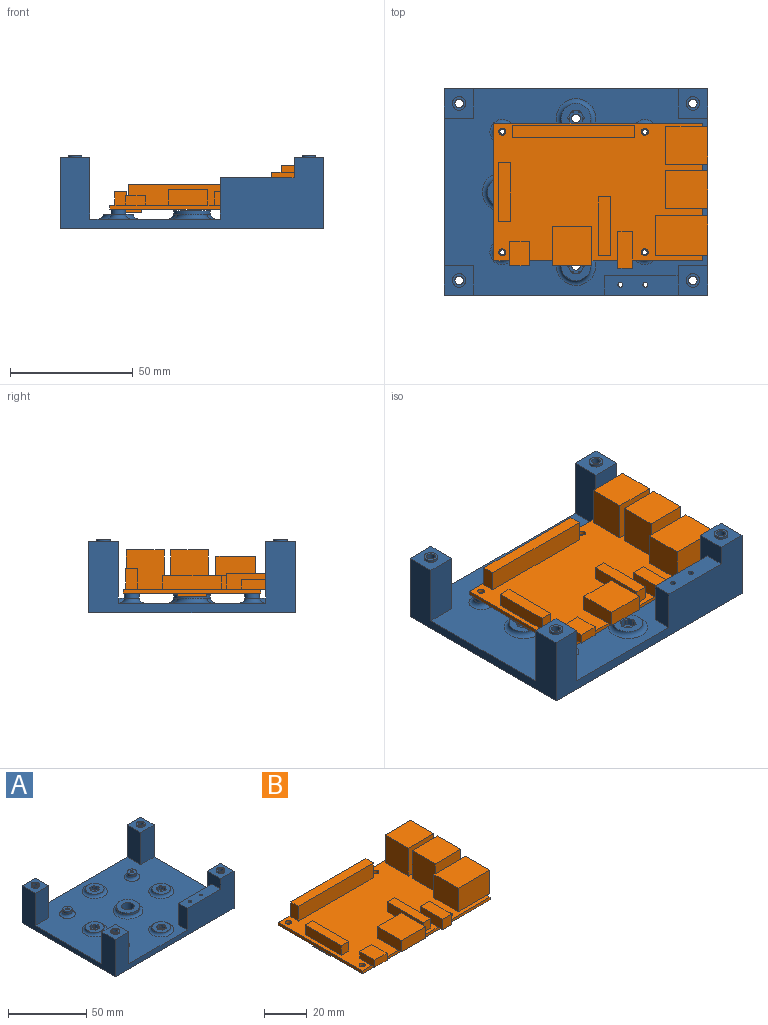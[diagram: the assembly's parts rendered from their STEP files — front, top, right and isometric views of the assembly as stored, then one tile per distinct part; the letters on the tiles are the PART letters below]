
ASSEMBLY  parts=2 mates=1
PART A: 277 faces, bbox 107x84x30 mm
  f0: plane 107x84mm, normal (0,0,1), area 6770.1mm2, adj f1,f2,f3,f4,f9,f24,f55,f56
  f1: plane 25x12mm, normal (-1,0,0), area 165.6mm2, adj f0,f4,f23,f24,f272,f274
  f2: plane 107x29mm, normal (0,1,0), area 1028mm2, adj f0,f3,f9,f10,f54,f55,f118,f119
  f3: plane 84x29mm, normal (-1,0,0), area 936mm2, adj f0,f2,f4,f10,f86,f88,f118,f120
  f4: plane 107x29mm, normal (0,-1,0), area 1532mm2, adj f0,f1,f3,f9,f10,f23,f86,f87
  f5: cylinder r=1mm len=8mm, axis (0,0,1), area 50.3mm2, adj f10,f11
  f6: cylinder r=1mm len=8mm, axis (0,0,1), area 50.3mm2, adj f10,f17
  f7: cylinder r=1mm len=8mm, axis (0,0,1), area 50.3mm2, adj f10,f13
  f8: cylinder r=1mm len=8mm, axis (0,0,1), area 50.3mm2, adj f10,f15
  f9: plane 84x29mm, normal (1,0,0), area 936mm2, adj f0,f2,f4,f10,f23,f24,f54,f56
  f10: plane 107x84mm, normal (0,0,-1), area 8651.1mm2, adj f2,f3,f4,f5,f6,f7,f8,f9
  f11: plane 6x6mm, normal (0,0,1), area 25.1mm2, adj f5,f12
  f12: cylinder r=3mm len=6mm, axis (0,0,-1), area 37.7mm2, adj f11,f263
  f13: plane 6x6mm, normal (0,0,1), area 25.1mm2, adj f7,f14
  f14: cylinder r=3mm len=6mm, axis (0,0,-1), area 37.7mm2, adj f13,f266
  f15: plane 6x6mm, normal (0,0,1), area 25.1mm2, adj f8,f16
  f16: cylinder r=3mm len=6mm, axis (0,0,-1), area 37.7mm2, adj f15,f265
  f17: plane 6x6mm, normal (0,0,1), area 25.1mm2, adj f6,f18
  f18: cylinder r=3mm len=6mm, axis (0,0,-1), area 37.7mm2, adj f17,f264
  f19: cylinder r=4mm len=22mm, axis (0,0,-1), area 552.9mm2, adj f10,f83
  f20: cylinder r=4mm len=22mm, axis (0,0,-1), area 552.9mm2, adj f10,f115
  f21: cylinder r=4mm len=22mm, axis (0,0,-1), area 552.9mm2, adj f10,f147
  f22: cylinder r=4mm len=22mm, axis (0,0,-1), area 552.9mm2, adj f10,f51
  f23: plane 12x12mm, normal (0,0,1), area 120.2mm2, adj f1,f4,f9,f24,f52
  f24: plane 25x12mm, normal (0,1,0), area 300mm2, adj f0,f1,f9,f23
  f25: plane 3x2.96mm, normal (0,1,0), area 6.4mm2, adj f31,f32,f33,f40,f41,f42,f49,f51
  f26: plane 3x2.57mm, normal (-0.87,0.5,0), area 6.4mm2, adj f31,f32,f33,f37,f38,f39,f49,f51
  f27: plane 3x2.57mm, normal (-0.87,-0.5,0), area 6.4mm2, adj f34,f35,f36,f37,f38,f39,f49,f51
  f28: plane 3x2.96mm, normal (0,-1,0), area 6.4mm2, adj f34,f35,f36,f46,f47,f48,f49,f51
  f29: plane 3x2.57mm, normal (0.87,-0.5,0), area 6.4mm2, adj f43,f44,f45,f46,f47,f48,f49,f51
  f30: plane 3x2.57mm, normal (0.87,0.5,0), area 6.4mm2, adj f40,f41,f42,f43,f44,f45,f49,f51
  f31: cylinder r=0.75mm len=2mm, axis (0,0,-1), area 3.1mm2, adj f25,f26,f32,f33
  f32: cone r=0.25mm half-angle=45deg, axis (0,0,-1), area 0.7mm2, adj f25,f26,f31,f49
  f33: cone r=0.75mm half-angle=45deg, axis (0,0,1), area 0.7mm2, adj f25,f26,f31,f51
  f34: cylinder r=0.75mm len=2mm, axis (0,0,-1), area 3.1mm2, adj f27,f28,f35,f36
  f35: cone r=0.25mm half-angle=45deg, axis (0,0,-1), area 0.7mm2, adj f27,f28,f34,f49
  f36: cone r=0.75mm half-angle=45deg, axis (0,0,1), area 0.7mm2, adj f27,f28,f34,f51
  f37: cone r=0.75mm half-angle=45deg, axis (0,0,1), area 0.7mm2, adj f26,f27,f39,f51
  f38: cone r=0.25mm half-angle=45deg, axis (0,0,-1), area 0.7mm2, adj f26,f27,f39,f49
  f39: cylinder r=0.75mm len=2mm, axis (0,0,-1), area 3.1mm2, adj f26,f27,f37,f38
  f40: cone r=0.75mm half-angle=45deg, axis (0,0,1), area 0.7mm2, adj f25,f30,f42,f51
  f41: cone r=0.25mm half-angle=45deg, axis (0,0,-1), area 0.7mm2, adj f25,f30,f42,f49
  f42: cylinder r=0.75mm len=2mm, axis (0,0,-1), area 3.1mm2, adj f25,f30,f40,f41
  f43: cone r=0.75mm half-angle=45deg, axis (0,0,1), area 0.7mm2, adj f29,f30,f45,f51
  f44: cone r=0.25mm half-angle=45deg, axis (0,0,-1), area 0.7mm2, adj f29,f30,f45,f49
  f45: cylinder r=0.75mm len=2mm, axis (0,0,-1), area 3.1mm2, adj f29,f30,f43,f44
  f46: cone r=0.75mm half-angle=45deg, axis (0,0,1), area 0.7mm2, adj f28,f29,f48,f51
  f47: cone r=0.25mm half-angle=45deg, axis (0,0,-1), area 0.7mm2, adj f28,f29,f48,f49
  f48: cylinder r=0.75mm len=2mm, axis (0,0,-1), area 3.1mm2, adj f28,f29,f46,f47
  f49: plane 6.68x6mm, normal (0,0,-1), area 21.2mm2, adj f25,f26,f27,f28,f29,f30,f32,f35
  f50: cylinder r=1.75mm len=5mm, axis (0,0,1), area 55mm2, adj f49,f53
  f51: plane 8x8mm, normal (0,0,-1), area 19.5mm2, adj f22,f25,f26,f27,f28,f29,f30,f33
  f52: cylinder r=2.75mm len=5.5mm, axis (0,0,-1), area 17.3mm2, adj f23,f53
  f53: plane 5.5x5.5mm, normal (0,0,1), area 14.1mm2, adj f50,f52
  f54: plane 12x12mm, normal (0,0,1), area 120.2mm2, adj f2,f9,f55,f56,f84
  f55: plane 25x12mm, normal (-1,0,0), area 300mm2, adj f0,f2,f54,f56
  f56: plane 25x12mm, normal (0,-1,0), area 300mm2, adj f0,f9,f54,f55
  f57: plane 3x2.96mm, normal (0,-1,0), area 6.4mm2, adj f63,f64,f65,f72,f73,f74,f81,f83
  f58: plane 3x2.57mm, normal (-0.87,-0.5,0), area 6.4mm2, adj f63,f64,f65,f69,f70,f71,f81,f83
  f59: plane 3x2.57mm, normal (-0.87,0.5,0), area 6.4mm2, adj f66,f67,f68,f69,f70,f71,f81,f83
  f60: plane 3x2.96mm, normal (0,1,0), area 6.4mm2, adj f66,f67,f68,f78,f79,f80,f81,f83
  f61: plane 3x2.57mm, normal (0.87,0.5,0), area 6.4mm2, adj f75,f76,f77,f78,f79,f80,f81,f83
  f62: plane 3x2.57mm, normal (0.87,-0.5,0), area 6.4mm2, adj f72,f73,f74,f75,f76,f77,f81,f83
  f63: cylinder r=0.75mm len=2mm, axis (0,0,-1), area 3.1mm2, adj f57,f58,f64,f65
  f64: cone r=0.25mm half-angle=45deg, axis (0,0,-1), area 0.7mm2, adj f57,f58,f63,f81
  f65: cone r=0.75mm half-angle=45deg, axis (0,0,1), area 0.7mm2, adj f57,f58,f63,f83
  f66: cylinder r=0.75mm len=2mm, axis (0,0,-1), area 3.1mm2, adj f59,f60,f67,f68
  f67: cone r=0.25mm half-angle=45deg, axis (0,0,-1), area 0.7mm2, adj f59,f60,f66,f81
  f68: cone r=0.75mm half-angle=45deg, axis (0,0,1), area 0.7mm2, adj f59,f60,f66,f83
  f69: cone r=0.75mm half-angle=45deg, axis (0,0,1), area 0.7mm2, adj f58,f59,f71,f83
  f70: cone r=0.25mm half-angle=45deg, axis (0,0,-1), area 0.7mm2, adj f58,f59,f71,f81
  f71: cylinder r=0.75mm len=2mm, axis (0,0,-1), area 3.1mm2, adj f58,f59,f69,f70
  f72: cone r=0.75mm half-angle=45deg, axis (0,0,1), area 0.7mm2, adj f57,f62,f74,f83
  f73: cone r=0.25mm half-angle=45deg, axis (0,0,-1), area 0.7mm2, adj f57,f62,f74,f81
  f74: cylinder r=0.75mm len=2mm, axis (0,0,-1), area 3.1mm2, adj f57,f62,f72,f73
  f75: cone r=0.75mm half-angle=45deg, axis (0,0,1), area 0.7mm2, adj f61,f62,f77,f83
  f76: cone r=0.25mm half-angle=45deg, axis (0,0,-1), area 0.7mm2, adj f61,f62,f77,f81
  f77: cylinder r=0.75mm len=2mm, axis (0,0,-1), area 3.1mm2, adj f61,f62,f75,f76
  f78: cone r=0.75mm half-angle=45deg, axis (0,0,1), area 0.7mm2, adj f60,f61,f80,f83
  f79: cone r=0.25mm half-angle=45deg, axis (0,0,-1), area 0.7mm2, adj f60,f61,f80,f81
  f80: cylinder r=0.75mm len=2mm, axis (0,0,-1), area 3.1mm2, adj f60,f61,f78,f79
  f81: plane 6.68x6mm, normal (0,0,-1), area 21.2mm2, adj f57,f58,f59,f60,f61,f62,f64,f67
  f82: cylinder r=1.75mm len=5mm, axis (0,0,1), area 55mm2, adj f81,f85
  f83: plane 8x8mm, normal (0,0,-1), area 19.5mm2, adj f19,f57,f58,f59,f60,f61,f62,f65
  f84: cylinder r=2.75mm len=5.5mm, axis (0,0,-1), area 17.3mm2, adj f54,f85
  f85: plane 5.5x5.5mm, normal (0,0,1), area 14.1mm2, adj f82,f84
  f86: plane 12x12mm, normal (0,0,1), area 120.2mm2, adj f3,f4,f87,f88,f116
  f87: plane 25x12mm, normal (1,0,0), area 300mm2, adj f0,f4,f86,f88
  f88: plane 25x12mm, normal (0,1,0), area 300mm2, adj f0,f3,f86,f87
  f89: plane 3x2.96mm, normal (0,1,0), area 6.4mm2, adj f95,f96,f97,f104,f105,f106,f113,f115
  f90: plane 3x2.57mm, normal (0.87,0.5,0), area 6.4mm2, adj f95,f96,f97,f101,f102,f103,f113,f115
  f91: plane 3x2.57mm, normal (0.87,-0.5,0), area 6.4mm2, adj f98,f99,f100,f101,f102,f103,f113,f115
  f92: plane 3x2.96mm, normal (0,-1,0), area 6.4mm2, adj f98,f99,f100,f110,f111,f112,f113,f115
  f93: plane 3x2.57mm, normal (-0.87,-0.5,0), area 6.4mm2, adj f107,f108,f109,f110,f111,f112,f113,f115
  f94: plane 3x2.57mm, normal (-0.87,0.5,0), area 6.4mm2, adj f104,f105,f106,f107,f108,f109,f113,f115
  f95: cylinder r=0.75mm len=2mm, axis (0,0,-1), area 3.1mm2, adj f89,f90,f96,f97
  f96: cone r=0.25mm half-angle=45deg, axis (0,0,-1), area 0.7mm2, adj f89,f90,f95,f113
  f97: cone r=0.75mm half-angle=45deg, axis (0,0,1), area 0.7mm2, adj f89,f90,f95,f115
  f98: cylinder r=0.75mm len=2mm, axis (0,0,-1), area 3.1mm2, adj f91,f92,f99,f100
  f99: cone r=0.25mm half-angle=45deg, axis (0,0,-1), area 0.7mm2, adj f91,f92,f98,f113
  f100: cone r=0.75mm half-angle=45deg, axis (0,0,1), area 0.7mm2, adj f91,f92,f98,f115
  f101: cone r=0.75mm half-angle=45deg, axis (0,0,1), area 0.7mm2, adj f90,f91,f103,f115
  f102: cone r=0.25mm half-angle=45deg, axis (0,0,-1), area 0.7mm2, adj f90,f91,f103,f113
  f103: cylinder r=0.75mm len=2mm, axis (0,0,-1), area 3.1mm2, adj f90,f91,f101,f102
  f104: cone r=0.75mm half-angle=45deg, axis (0,0,1), area 0.7mm2, adj f89,f94,f106,f115
  f105: cone r=0.25mm half-angle=45deg, axis (0,0,-1), area 0.7mm2, adj f89,f94,f106,f113
  f106: cylinder r=0.75mm len=2mm, axis (0,0,-1), area 3.1mm2, adj f89,f94,f104,f105
  f107: cone r=0.75mm half-angle=45deg, axis (0,0,1), area 0.7mm2, adj f93,f94,f109,f115
  f108: cone r=0.25mm half-angle=45deg, axis (0,0,-1), area 0.7mm2, adj f93,f94,f109,f113
  f109: cylinder r=0.75mm len=2mm, axis (0,0,-1), area 3.1mm2, adj f93,f94,f107,f108
  f110: cone r=0.75mm half-angle=45deg, axis (0,0,1), area 0.7mm2, adj f92,f93,f112,f115
  f111: cone r=0.25mm half-angle=45deg, axis (0,0,-1), area 0.7mm2, adj f92,f93,f112,f113
  f112: cylinder r=0.75mm len=2mm, axis (0,0,-1), area 3.1mm2, adj f92,f93,f110,f111
  f113: plane 6.68x6mm, normal (0,0,-1), area 21.2mm2, adj f89,f90,f91,f92,f93,f94,f96,f99
  f114: cylinder r=1.75mm len=5mm, axis (0,0,1), area 55mm2, adj f113,f117
  f115: plane 8x8mm, normal (0,0,-1), area 19.5mm2, adj f20,f89,f90,f91,f92,f93,f94,f97
  f116: cylinder r=2.75mm len=5.5mm, axis (0,0,-1), area 17.3mm2, adj f86,f117
  f117: plane 5.5x5.5mm, normal (0,0,1), area 14.1mm2, adj f114,f116
  f118: plane 12x12mm, normal (0,0,1), area 120.2mm2, adj f2,f3,f119,f120,f148
  f119: plane 25x12mm, normal (1,0,0), area 300mm2, adj f0,f2,f118,f120
  f120: plane 25x12mm, normal (0,-1,0), area 300mm2, adj f0,f3,f118,f119
  f121: plane 3x2.96mm, normal (0,-1,0), area 6.4mm2, adj f127,f128,f129,f136,f137,f138,f145,f147
  f122: plane 3x2.57mm, normal (0.87,-0.5,0), area 6.4mm2, adj f127,f128,f129,f133,f134,f135,f145,f147
  f123: plane 3x2.57mm, normal (0.87,0.5,0), area 6.4mm2, adj f130,f131,f132,f133,f134,f135,f145,f147
  f124: plane 3x2.96mm, normal (0,1,0), area 6.4mm2, adj f130,f131,f132,f142,f143,f144,f145,f147
  f125: plane 3x2.57mm, normal (-0.87,0.5,0), area 6.4mm2, adj f139,f140,f141,f142,f143,f144,f145,f147
  f126: plane 3x2.57mm, normal (-0.87,-0.5,0), area 6.4mm2, adj f136,f137,f138,f139,f140,f141,f145,f147
  f127: cylinder r=0.75mm len=2mm, axis (0,0,-1), area 3.1mm2, adj f121,f122,f128,f129
  f128: cone r=0.25mm half-angle=45deg, axis (0,0,-1), area 0.7mm2, adj f121,f122,f127,f145
  f129: cone r=0.75mm half-angle=45deg, axis (0,0,1), area 0.7mm2, adj f121,f122,f127,f147
  f130: cylinder r=0.75mm len=2mm, axis (0,0,-1), area 3.1mm2, adj f123,f124,f131,f132
  f131: cone r=0.25mm half-angle=45deg, axis (0,0,-1), area 0.7mm2, adj f123,f124,f130,f145
  f132: cone r=0.75mm half-angle=45deg, axis (0,0,1), area 0.7mm2, adj f123,f124,f130,f147
  f133: cone r=0.75mm half-angle=45deg, axis (0,0,1), area 0.7mm2, adj f122,f123,f135,f147
  f134: cone r=0.25mm half-angle=45deg, axis (0,0,-1), area 0.7mm2, adj f122,f123,f135,f145
  f135: cylinder r=0.75mm len=2mm, axis (0,0,-1), area 3.1mm2, adj f122,f123,f133,f134
  f136: cone r=0.75mm half-angle=45deg, axis (0,0,1), area 0.7mm2, adj f121,f126,f138,f147
  f137: cone r=0.25mm half-angle=45deg, axis (0,0,-1), area 0.7mm2, adj f121,f126,f138,f145
  f138: cylinder r=0.75mm len=2mm, axis (0,0,-1), area 3.1mm2, adj f121,f126,f136,f137
  f139: cone r=0.75mm half-angle=45deg, axis (0,0,1), area 0.7mm2, adj f125,f126,f141,f147
  f140: cone r=0.25mm half-angle=45deg, axis (0,0,-1), area 0.7mm2, adj f125,f126,f141,f145
  f141: cylinder r=0.75mm len=2mm, axis (0,0,-1), area 3.1mm2, adj f125,f126,f139,f140
  f142: cone r=0.75mm half-angle=45deg, axis (0,0,1), area 0.7mm2, adj f124,f125,f144,f147
  f143: cone r=0.25mm half-angle=45deg, axis (0,0,-1), area 0.7mm2, adj f124,f125,f144,f145
  f144: cylinder r=0.75mm len=2mm, axis (0,0,-1), area 3.1mm2, adj f124,f125,f142,f143
  f145: plane 6.68x6mm, normal (0,0,-1), area 21.2mm2, adj f121,f122,f123,f124,f125,f126,f128,f131
  f146: cylinder r=1.75mm len=5mm, axis (0,0,1), area 55mm2, adj f145,f149
  f147: plane 8x8mm, normal (0,0,-1), area 19.5mm2, adj f21,f121,f122,f123,f124,f125,f126,f129
  f148: cylinder r=2.75mm len=5.5mm, axis (0,0,-1), area 17.3mm2, adj f118,f149
  f149: plane 5.5x5.5mm, normal (0,0,1), area 14.1mm2, adj f146,f148
  f150: plane 15x15mm, normal (0,0,1), area 126.4mm2, adj f151,f152
  f151: cylinder r=7.5mm len=15mm, axis (0,0,1), area 61.3mm2, adj f150,f267
  f152: cylinder r=4mm len=8mm, axis (0,0,1), area 138.2mm2, adj f150,f153
  f153: plane 10x10mm, normal (0,0,-1), area 28.3mm2, adj f152,f154
  f154: cylinder r=5mm len=10mm, axis (0,0,1), area 56.5mm2, adj f10,f153
  f155: plane 12x12mm, normal (0,0,1), area 82.3mm2, adj f156,f157,f158,f159,f160,f161,f163,f166
  f156: plane 3x2.96mm, normal (0,-1,0), area 6.4mm2, adj f155,f162,f163,f164,f171,f172,f173,f180
  f157: plane 3x2.57mm, normal (-0.87,-0.5,0), area 6.4mm2, adj f155,f162,f163,f164,f168,f169,f170,f180
  f158: plane 3x2.57mm, normal (-0.87,0.5,0), area 6.4mm2, adj f155,f165,f166,f167,f168,f169,f170,f180
  f159: plane 3x2.96mm, normal (0,1,0), area 6.4mm2, adj f155,f165,f166,f167,f177,f178,f179,f180
  f160: plane 3x2.57mm, normal (0.87,0.5,0), area 6.4mm2, adj f155,f174,f175,f176,f177,f178,f179,f180
  f161: plane 3x2.57mm, normal (0.87,-0.5,0), area 6.4mm2, adj f155,f171,f172,f173,f174,f175,f176,f180
  f162: cylinder r=0.75mm len=2mm, axis (0,0,-1), area 3.1mm2, adj f156,f157,f163,f164
  f163: cone r=0.25mm half-angle=45deg, axis (0,0,-1), area 0.7mm2, adj f155,f156,f157,f162
  f164: cone r=0.75mm half-angle=45deg, axis (0,0,1), area 0.7mm2, adj f156,f157,f162,f180
  f165: cylinder r=0.75mm len=2mm, axis (0,0,-1), area 3.1mm2, adj f158,f159,f166,f167
  f166: cone r=0.25mm half-angle=45deg, axis (0,0,-1), area 0.7mm2, adj f155,f158,f159,f165
  f167: cone r=0.75mm half-angle=45deg, axis (0,0,1), area 0.7mm2, adj f158,f159,f165,f180
  f168: cone r=0.75mm half-angle=45deg, axis (0,0,1), area 0.7mm2, adj f157,f158,f170,f180
  f169: cone r=0.25mm half-angle=45deg, axis (0,0,-1), area 0.7mm2, adj f155,f157,f158,f170
  f170: cylinder r=0.75mm len=2mm, axis (0,0,-1), area 3.1mm2, adj f157,f158,f168,f169
  f171: cone r=0.75mm half-angle=45deg, axis (0,0,1), area 0.7mm2, adj f156,f161,f173,f180
  f172: cone r=0.25mm half-angle=45deg, axis (0,0,-1), area 0.7mm2, adj f155,f156,f161,f173
  f173: cylinder r=0.75mm len=2mm, axis (0,0,-1), area 3.1mm2, adj f156,f161,f171,f172
  f174: cone r=0.75mm half-angle=45deg, axis (0,0,1), area 0.7mm2, adj f160,f161,f176,f180
  f175: cone r=0.25mm half-angle=45deg, axis (0,0,-1), area 0.7mm2, adj f155,f160,f161,f176
  f176: cylinder r=0.75mm len=2mm, axis (0,0,-1), area 3.1mm2, adj f160,f161,f174,f175
  f177: cone r=0.75mm half-angle=45deg, axis (0,0,1), area 0.7mm2, adj f159,f160,f179,f180
  f178: cone r=0.25mm half-angle=45deg, axis (0,0,-1), area 0.7mm2, adj f155,f159,f160,f179
  f179: cylinder r=0.75mm len=2mm, axis (0,0,-1), area 3.1mm2, adj f159,f160,f177,f178
  f180: plane 6.68x6mm, normal (0,0,1), area 21.2mm2, adj f156,f157,f158,f159,f160,f161,f164,f167
  f181: cylinder r=1.75mm len=3.5mm, axis (0,0,-1), area 33mm2, adj f10,f180
  f182: plane 12x12mm, normal (0,0,1), area 82.3mm2, adj f183,f184,f185,f186,f187,f188,f190,f193
  f183: plane 3x2.96mm, normal (0,-1,0), area 6.4mm2, adj f182,f189,f190,f191,f198,f199,f200,f207
  f184: plane 3x2.57mm, normal (-0.87,-0.5,0), area 6.4mm2, adj f182,f189,f190,f191,f195,f196,f197,f207
  f185: plane 3x2.57mm, normal (-0.87,0.5,0), area 6.4mm2, adj f182,f192,f193,f194,f195,f196,f197,f207
  f186: plane 3x2.96mm, normal (0,1,0), area 6.4mm2, adj f182,f192,f193,f194,f204,f205,f206,f207
  f187: plane 3x2.57mm, normal (0.87,0.5,0), area 6.4mm2, adj f182,f201,f202,f203,f204,f205,f206,f207
  f188: plane 3x2.57mm, normal (0.87,-0.5,0), area 6.4mm2, adj f182,f198,f199,f200,f201,f202,f203,f207
  f189: cylinder r=0.75mm len=2mm, axis (0,0,-1), area 3.1mm2, adj f183,f184,f190,f191
  f190: cone r=0.25mm half-angle=45deg, axis (0,0,-1), area 0.7mm2, adj f182,f183,f184,f189
  f191: cone r=0.75mm half-angle=45deg, axis (0,0,1), area 0.7mm2, adj f183,f184,f189,f207
  f192: cylinder r=0.75mm len=2mm, axis (0,0,-1), area 3.1mm2, adj f185,f186,f193,f194
  f193: cone r=0.25mm half-angle=45deg, axis (0,0,-1), area 0.7mm2, adj f182,f185,f186,f192
  f194: cone r=0.75mm half-angle=45deg, axis (0,0,1), area 0.7mm2, adj f185,f186,f192,f207
  f195: cone r=0.75mm half-angle=45deg, axis (0,0,1), area 0.7mm2, adj f184,f185,f197,f207
  f196: cone r=0.25mm half-angle=45deg, axis (0,0,-1), area 0.7mm2, adj f182,f184,f185,f197
  f197: cylinder r=0.75mm len=2mm, axis (0,0,-1), area 3.1mm2, adj f184,f185,f195,f196
  f198: cone r=0.75mm half-angle=45deg, axis (0,0,1), area 0.7mm2, adj f183,f188,f200,f207
  f199: cone r=0.25mm half-angle=45deg, axis (0,0,-1), area 0.7mm2, adj f182,f183,f188,f200
  f200: cylinder r=0.75mm len=2mm, axis (0,0,-1), area 3.1mm2, adj f183,f188,f198,f199
  f201: cone r=0.75mm half-angle=45deg, axis (0,0,1), area 0.7mm2, adj f187,f188,f203,f207
  f202: cone r=0.25mm half-angle=45deg, axis (0,0,-1), area 0.7mm2, adj f182,f187,f188,f203
  f203: cylinder r=0.75mm len=2mm, axis (0,0,-1), area 3.1mm2, adj f187,f188,f201,f202
  f204: cone r=0.75mm half-angle=45deg, axis (0,0,1), area 0.7mm2, adj f186,f187,f206,f207
  f205: cone r=0.25mm half-angle=45deg, axis (0,0,-1), area 0.7mm2, adj f182,f186,f187,f206
  f206: cylinder r=0.75mm len=2mm, axis (0,0,-1), area 3.1mm2, adj f186,f187,f204,f205
  f207: plane 6.68x6mm, normal (0,0,1), area 21.2mm2, adj f183,f184,f185,f186,f187,f188,f191,f194
  f208: cylinder r=1.75mm len=3.5mm, axis (0,0,-1), area 33mm2, adj f10,f207
  f209: plane 12x12mm, normal (0,0,1), area 82.3mm2, adj f210,f211,f212,f213,f214,f215,f217,f220
  f210: plane 3x2.96mm, normal (0,-1,0), area 6.4mm2, adj f209,f216,f217,f218,f225,f226,f227,f234
  f211: plane 3x2.57mm, normal (-0.87,-0.5,0), area 6.4mm2, adj f209,f216,f217,f218,f222,f223,f224,f234
  f212: plane 3x2.57mm, normal (-0.87,0.5,0), area 6.4mm2, adj f209,f219,f220,f221,f222,f223,f224,f234
  f213: plane 3x2.96mm, normal (0,1,0), area 6.4mm2, adj f209,f219,f220,f221,f231,f232,f233,f234
  f214: plane 3x2.57mm, normal (0.87,0.5,0), area 6.4mm2, adj f209,f228,f229,f230,f231,f232,f233,f234
  f215: plane 3x2.57mm, normal (0.87,-0.5,0), area 6.4mm2, adj f209,f225,f226,f227,f228,f229,f230,f234
  f216: cylinder r=0.75mm len=2mm, axis (0,0,-1), area 3.1mm2, adj f210,f211,f217,f218
  f217: cone r=0.25mm half-angle=45deg, axis (0,0,-1), area 0.7mm2, adj f209,f210,f211,f216
  f218: cone r=0.75mm half-angle=45deg, axis (0,0,1), area 0.7mm2, adj f210,f211,f216,f234
  f219: cylinder r=0.75mm len=2mm, axis (0,0,-1), area 3.1mm2, adj f212,f213,f220,f221
  f220: cone r=0.25mm half-angle=45deg, axis (0,0,-1), area 0.7mm2, adj f209,f212,f213,f219
  f221: cone r=0.75mm half-angle=45deg, axis (0,0,1), area 0.7mm2, adj f212,f213,f219,f234
  f222: cone r=0.75mm half-angle=45deg, axis (0,0,1), area 0.7mm2, adj f211,f212,f224,f234
  f223: cone r=0.25mm half-angle=45deg, axis (0,0,-1), area 0.7mm2, adj f209,f211,f212,f224
  f224: cylinder r=0.75mm len=2mm, axis (0,0,-1), area 3.1mm2, adj f211,f212,f222,f223
  f225: cone r=0.75mm half-angle=45deg, axis (0,0,1), area 0.7mm2, adj f210,f215,f227,f234
  f226: cone r=0.25mm half-angle=45deg, axis (0,0,-1), area 0.7mm2, adj f209,f210,f215,f227
  f227: cylinder r=0.75mm len=2mm, axis (0,0,-1), area 3.1mm2, adj f210,f215,f225,f226
  f228: cone r=0.75mm half-angle=45deg, axis (0,0,1), area 0.7mm2, adj f214,f215,f230,f234
  f229: cone r=0.25mm half-angle=45deg, axis (0,0,-1), area 0.7mm2, adj f209,f214,f215,f230
  f230: cylinder r=0.75mm len=2mm, axis (0,0,-1), area 3.1mm2, adj f214,f215,f228,f229
  f231: cone r=0.75mm half-angle=45deg, axis (0,0,1), area 0.7mm2, adj f213,f214,f233,f234
  f232: cone r=0.25mm half-angle=45deg, axis (0,0,-1), area 0.7mm2, adj f209,f213,f214,f233
  f233: cylinder r=0.75mm len=2mm, axis (0,0,-1), area 3.1mm2, adj f213,f214,f231,f232
  f234: plane 6.68x6mm, normal (0,0,1), area 21.2mm2, adj f210,f211,f212,f213,f214,f215,f218,f221
  f235: cylinder r=1.75mm len=3.5mm, axis (0,0,-1), area 33mm2, adj f10,f234
  f236: plane 12x12mm, normal (0,0,1), area 82.3mm2, adj f237,f238,f239,f240,f241,f242,f244,f247
  f237: plane 3x2.96mm, normal (0,-1,0), area 6.4mm2, adj f236,f243,f244,f245,f252,f253,f254,f261
  f238: plane 3x2.57mm, normal (-0.87,-0.5,0), area 6.4mm2, adj f236,f243,f244,f245,f249,f250,f251,f261
  f239: plane 3x2.57mm, normal (-0.87,0.5,0), area 6.4mm2, adj f236,f246,f247,f248,f249,f250,f251,f261
  f240: plane 3x2.96mm, normal (0,1,0), area 6.4mm2, adj f236,f246,f247,f248,f258,f259,f260,f261
  f241: plane 3x2.57mm, normal (0.87,0.5,0), area 6.4mm2, adj f236,f255,f256,f257,f258,f259,f260,f261
  f242: plane 3x2.57mm, normal (0.87,-0.5,0), area 6.4mm2, adj f236,f252,f253,f254,f255,f256,f257,f261
  f243: cylinder r=0.75mm len=2mm, axis (0,0,-1), area 3.1mm2, adj f237,f238,f244,f245
  f244: cone r=0.25mm half-angle=45deg, axis (0,0,-1), area 0.7mm2, adj f236,f237,f238,f243
  f245: cone r=0.75mm half-angle=45deg, axis (0,0,1), area 0.7mm2, adj f237,f238,f243,f261
  f246: cylinder r=0.75mm len=2mm, axis (0,0,-1), area 3.1mm2, adj f239,f240,f247,f248
  f247: cone r=0.25mm half-angle=45deg, axis (0,0,-1), area 0.7mm2, adj f236,f239,f240,f246
  f248: cone r=0.75mm half-angle=45deg, axis (0,0,1), area 0.7mm2, adj f239,f240,f246,f261
  f249: cone r=0.75mm half-angle=45deg, axis (0,0,1), area 0.7mm2, adj f238,f239,f251,f261
  f250: cone r=0.25mm half-angle=45deg, axis (0,0,-1), area 0.7mm2, adj f236,f238,f239,f251
  f251: cylinder r=0.75mm len=2mm, axis (0,0,-1), area 3.1mm2, adj f238,f239,f249,f250
  f252: cone r=0.75mm half-angle=45deg, axis (0,0,1), area 0.7mm2, adj f237,f242,f254,f261
  f253: cone r=0.25mm half-angle=45deg, axis (0,0,-1), area 0.7mm2, adj f236,f237,f242,f254
  f254: cylinder r=0.75mm len=2mm, axis (0,0,-1), area 3.1mm2, adj f237,f242,f252,f253
  f255: cone r=0.75mm half-angle=45deg, axis (0,0,1), area 0.7mm2, adj f241,f242,f257,f261
  f256: cone r=0.25mm half-angle=45deg, axis (0,0,-1), area 0.7mm2, adj f236,f241,f242,f257
  f257: cylinder r=0.75mm len=2mm, axis (0,0,-1), area 3.1mm2, adj f241,f242,f255,f256
  f258: cone r=0.75mm half-angle=45deg, axis (0,0,1), area 0.7mm2, adj f240,f241,f260,f261
  f259: cone r=0.25mm half-angle=45deg, axis (0,0,-1), area 0.7mm2, adj f236,f240,f241,f260
  f260: cylinder r=0.75mm len=2mm, axis (0,0,-1), area 3.1mm2, adj f240,f241,f258,f259
  f261: plane 6.68x6mm, normal (0,0,1), area 21.2mm2, adj f237,f238,f239,f240,f241,f242,f245,f248
  f262: cylinder r=1.75mm len=3.5mm, axis (0,0,-1), area 33mm2, adj f10,f261
  f263: torus R=5mm, axis (0,0,1), area 73.6mm2, adj f0,f12
  f264: torus R=5mm, axis (0,0,1), area 73.6mm2, adj f0,f18
  f265: torus R=5mm, axis (0,0,1), area 73.6mm2, adj f0,f16
  f266: torus R=5mm, axis (0,0,1), area 73.6mm2, adj f0,f14
  f267: torus R=9.5mm, axis (0,0,1), area 162.4mm2, adj f0,f151
  f268: torus R=8mm, axis (0,0,1), area 132.8mm2, adj f0,f209
  f269: torus R=8mm, axis (0,0,1), area 132.8mm2, adj f0,f236
  f270: torus R=8mm, axis (0,0,1), area 132.8mm2, adj f0,f182
  f271: torus R=8mm, axis (0,0,1), area 132.8mm2, adj f0,f155
  f272: plane 30x16.8mm, normal (0,1,0), area 504mm2, adj f0,f1,f273,f274
  f273: plane 16.8x8mm, normal (-1,0,0), area 134.4mm2, adj f0,f4,f272,f274
  f274: plane 30x8mm, normal (0,0,1), area 233.7mm2, adj f1,f4,f272,f273,f275,f276
  f275: cylinder r=1mm len=20.8mm, axis (0,0,1), area 130.7mm2, adj f10,f274
  f276: cylinder r=1mm len=20.8mm, axis (0,0,1), area 130.7mm2, adj f10,f274
PART B: 66 faces, bbox 87x59x19.1 mm
  f0: plane 85x56mm, normal (0,0,1), area 3119.4mm2, adj f1,f2,f3,f4,f5,f6,f7,f8
  f1: plane 56x1.6mm, normal (1,0,0), area 89.6mm2, adj f0,f2,f7,f9,f15,f21,f27
  f2: plane 85x1.6mm, normal (0,1,0), area 136mm2, adj f0,f1,f3,f9
  f3: plane 56x1.6mm, normal (-1,0,0), area 89.6mm2, adj f0,f2,f7,f9
  f4: cylinder r=1.4mm len=2.8mm, axis (0,0,-1), area 14.1mm2, adj f0,f9
  f5: cylinder r=1.4mm len=2.8mm, axis (0,0,-1), area 14.1mm2, adj f0,f9
  f6: cylinder r=1.4mm len=2.8mm, axis (0,0,-1), area 14.1mm2, adj f0,f9
  f7: plane 85x1.6mm, normal (0,-1,0), area 136mm2, adj f0,f1,f3,f9,f33,f49,f60
  f8: cylinder r=1.4mm len=2.8mm, axis (0,0,-1), area 14.1mm2, adj f0,f9
  f9: plane 85x56mm, normal (0,0,-1), area 4591.4mm2, adj f1,f2,f3,f4,f5,f6,f7,f8
  f10: plane 21x13.5mm, normal (0,1,0), area 283.5mm2, adj f0,f11,f13,f14,f15
  f11: plane 16x13.5mm, normal (-1,0,0), area 216mm2, adj f0,f10,f12,f14
  f12: plane 21x13.5mm, normal (0,-1,0), area 283.5mm2, adj f0,f11,f13,f14,f15
  f13: plane 16x13.5mm, normal (1,0,0), area 216mm2, adj f10,f12,f14,f15
  f14: plane 21x16mm, normal (0,0,1), area 336mm2, adj f10,f11,f12,f13
  f15: plane 16x2mm, normal (0,0,-1), area 32mm2, adj f1,f10,f12,f13
  f16: plane 17x16mm, normal (0,1,0), area 272mm2, adj f0,f17,f19,f20,f21
  f17: plane 16x15.4mm, normal (-1,0,0), area 246.4mm2, adj f0,f16,f18,f20
  f18: plane 17x16mm, normal (0,-1,0), area 272mm2, adj f0,f17,f19,f20,f21
  f19: plane 16x15.4mm, normal (1,0,0), area 246.4mm2, adj f16,f18,f20,f21
  f20: plane 17x15.4mm, normal (0,0,1), area 261.8mm2, adj f16,f17,f18,f19
  f21: plane 15.4x2mm, normal (0,0,-1), area 30.8mm2, adj f1,f16,f18,f19
  f22: plane 17x16mm, normal (0,1,0), area 272mm2, adj f0,f23,f25,f26,f27
  f23: plane 16x15.4mm, normal (-1,0,0), area 246.4mm2, adj f0,f22,f24,f26
  f24: plane 17x16mm, normal (0,-1,0), area 272mm2, adj f0,f23,f25,f26,f27
  f25: plane 16x15.4mm, normal (1,0,0), area 246.4mm2, adj f22,f24,f26,f27
  f26: plane 17x15.4mm, normal (0,0,1), area 261.8mm2, adj f22,f23,f24,f25
  f27: plane 15.4x2mm, normal (0,0,-1), area 30.8mm2, adj f1,f22,f24,f25
  f28: plane 16x6.5mm, normal (1,0,0), area 104mm2, adj f0,f29,f31,f32,f33
  f29: plane 16x6.5mm, normal (0,1,0), area 104mm2, adj f0,f28,f30,f32
  f30: plane 16x6.5mm, normal (-1,0,0), area 104mm2, adj f0,f29,f31,f32,f33
  f31: plane 16x6.5mm, normal (0,-1,0), area 104mm2, adj f28,f30,f32,f33
  f32: plane 16x16mm, normal (0,0,1), area 256mm2, adj f28,f29,f30,f31
  f33: plane 16x2mm, normal (0,0,-1), area 32mm2, adj f7,f28,f30,f31
  f34: plane 50x8.5mm, normal (0,-1,0), area 425mm2, adj f0,f35,f37,f38
  f35: plane 8.5x5mm, normal (1,0,0), area 42.5mm2, adj f0,f34,f36,f38
  f36: plane 50x8.5mm, normal (0,1,0), area 425mm2, adj f0,f35,f37,f38
  f37: plane 8.5x5mm, normal (-1,0,0), area 42.5mm2, adj f0,f34,f36,f38
  f38: plane 50x5mm, normal (0,0,1), area 250mm2, adj f34,f35,f36,f37
  f39: plane 24x5.5mm, normal (1,0,0), area 132mm2, adj f0,f40,f42,f43
  f40: plane 5.5x5mm, normal (0,1,0), area 27.5mm2, adj f0,f39,f41,f43
  f41: plane 24x5.5mm, normal (-1,0,0), area 132mm2, adj f0,f40,f42,f43
  f42: plane 5.5x5mm, normal (0,-1,0), area 27.5mm2, adj f0,f39,f41,f43
  f43: plane 24x5mm, normal (0,0,1), area 120mm2, adj f39,f40,f41,f42
  f44: plane 8x4mm, normal (0,-1,0), area 32mm2, adj f45,f47,f48,f49
  f45: plane 10x4mm, normal (1,0,0), area 40mm2, adj f0,f44,f46,f48,f49
  f46: plane 8x4mm, normal (0,1,0), area 32mm2, adj f0,f45,f47,f48
  f47: plane 10x4mm, normal (-1,0,0), area 40mm2, adj f0,f44,f46,f48,f49
  f48: plane 10x8mm, normal (0,0,1), area 80mm2, adj f44,f45,f46,f47
  f49: plane 8x2mm, normal (0,0,-1), area 16mm2, adj f7,f44,f45,f47
  f50: plane 5.5x5mm, normal (0,1,0), area 27.5mm2, adj f0,f51,f53,f54
  f51: plane 24x5.5mm, normal (-1,0,0), area 132mm2, adj f0,f50,f52,f54
  f52: plane 5.5x5mm, normal (0,-1,0), area 27.5mm2, adj f0,f51,f53,f54
  f53: plane 24x5.5mm, normal (1,0,0), area 132mm2, adj f0,f50,f52,f54
  f54: plane 24x5mm, normal (0,0,1), area 120mm2, adj f50,f51,f52,f53
  f55: plane 15x6mm, normal (1,0,0), area 90mm2, adj f0,f56,f58,f59,f60
  f56: plane 6x6mm, normal (0,1,0), area 36mm2, adj f0,f55,f57,f59
  f57: plane 15x6mm, normal (-1,0,0), area 90mm2, adj f0,f56,f58,f59,f60
  f58: plane 6x6mm, normal (0,-1,0), area 36mm2, adj f55,f57,f59,f60
  f59: plane 15x6mm, normal (0,0,1), area 90mm2, adj f55,f56,f57,f58
  f60: plane 6x3mm, normal (0,0,-1), area 18mm2, adj f7,f55,f57,f58
  f61: plane 12x1.5mm, normal (1,0,0), area 18mm2, adj f9,f62,f64,f65
  f62: plane 12x1.5mm, normal (0,-1,0), area 18mm2, adj f9,f61,f63,f65
  f63: plane 12x1.5mm, normal (-1,0,0), area 18mm2, adj f9,f62,f64,f65
  f64: plane 12x1.5mm, normal (0,1,0), area 18mm2, adj f9,f61,f63,f65
  f65: plane 12x12mm, normal (0,0,-1), area 144mm2, adj f61,f62,f63,f64
PLACE A at identity fixed
PLACE B t=(0,0,4)mm
MATE fastened A.f6 <-> B.f8  axis (0,0,1) through (-39,-24.5,4)mm
